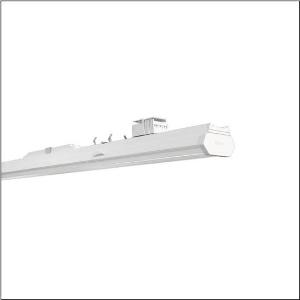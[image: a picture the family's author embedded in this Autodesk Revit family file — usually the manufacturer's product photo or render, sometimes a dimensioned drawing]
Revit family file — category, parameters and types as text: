
# Revit family: licross_r__11_protected_mo_51td1bdn49xg3s4_3b80
name_source: partatom
category: Lighting Fixtures
units: mm (PartAtom-declared; Revit-internal decimal feet)

## family parameters
Cut with Voids When Loaded = No
Host = Face
Light Source = No
Part Type = Normal
Room Calculation Point = No
Round Connector Dimension = Use Diameter
Shared = No

## types (1)
- --- (1 x LED, 920 lm, 6.8 W, 4000K)
    Apparent Load = 7 VA
    CIE Flux Codes = 54 82 95 97 100
    Color Rendering = 80
    Color Temperature = 4000K
    Default Elevation = 1800 mm
    Description = Licross® 11 Protected MO, luminaire insert, of sheet steel, galvanised, coil coated, white, length: 1.500mm, width: 90mm, height: 101mm, LED rated luminous flux: 9.370lm, light colour: 840, control gear: DALI 2, with plug, 6-pole, with phase selection, for trunking rail, 9 or 11-core, mains connection: 220..240V, AC, 50/60Hz, rated input power: 61W, for trunking rail, 9-/11-core, halogen-free wiring, for emergency light function, converter,control gear: single battery element, battery: LiFePO4, 9Ah, primary optical cover: cover, of PMMA, light emission: direct distribution, primary light characteristic: symmetric, protection rating (complete): IP54, insulation class (complete): insulation class I (protective earthing), certification: CE, UKCA, protection symbol: D if used in an environment with non-conductive dust loads with corresponding accessories, impact resistance: IK06, permissible ambient temperature for indoor applications: +5..+35°C, standard: EN 60598-2-22, LABS conformity tested according to VDMA 24364:2018-05, reducing of maximum allowable ambient temperature of 5°C with ceiling mounting, corresponds to IFS (International Featured Standards) requirements for safety and quality in the food industry, packaging unit: 1 piece
    Height = 92 mm
    Lamp = 1 x LED
    Lamp Light Flux = 920 lm
    Lamp Power = 6.8 W
    Lamp count = 1
    Length = 1500 mm
    Luminous efficacy = 135 lm/W
    Manufacturer = Siteco
    ModVariant = No
    Model = 51TD1BDN49XG3S4
    Mounting Place = Ceiling
    Mounting Type = Pendant
    Number of Poles = 1
    OnlyDefault = Yes
    Power Factor = 1
    Product Name = Licross® 11 Protected MO
    Product group = luminaire insert
    ProductGroupID = 901
    Protection Class = Protection class I
    Protection Degree = IP 54
    RLX_Detail_Level = 1
    RLX_Emergency_Light_Flux = 0 lm
    RLX_Emergency_Type = 0
    RLX_Emergency_Type_DB = No
    RlxData = <blob elided: 24569 chars, md5=f226d768>
    Socket = socket
    Standby Power = 0 W
    System Light Flux = 920 lm
    System Power = 7 W
    Type Comments = : emergency light operation: 3 h
    Type Image = l_1256145.jpg
    URL = http://relux.com
    VarID = @adj_059883
    Voltage = 0 V
    Weight = 0.00 kg
    Width = 88 mm

## geometry (parser evidence)
native form markers: Blend x4, Sweep x11
no freeform markers — native parametric forms only
